# Revit family: 3034751 Lighting Fixture_Sylvania_Giotto 235 LED_Recessed Mounted
name_source: partatom
category: Lighting Fixtures
revit_build: Autodesk Revit 2015 (Build: 20140606_1530(x64)
units: mm (PartAtom-declared; Revit-internal decimal feet)

## types (1)
- Giotto235 rec ww EB
    Apparent Load = 12 VA
    Assembly Code = D5020200
    Body Material = Polycarbonate_Sylvania_Giotto_White
    Catalog Number = 3034751
    Color Filter = 16777215
    Cutout Diameter = 235 mm
    Default Elevation = 0 mm  [stored 0 ft]
    Description = Surface or recessed mount versions available Ideal for general lighting in public areas Microwave presence detection versions 3 hour emergency light versions with integrated gear Up to 1200lm neutral white
    Diffuser Material = Polycarbonate_Sylvania_Giotto_Opal
    Dimming Lamp Color Temperature Shift = <None>
    Drive Current = 700 mA
    Electrical Protection = CLASS I
    Emit Shape Visible in Rendering = No
    Emit from Circle Diameter = 219 mm
    Energy Class = A++A+A
    Glow Wire Test = 850 °C
    Height = 92 mm  [stored 0.301837 ft]
    IK Rating = IK10
    IP Rating = IP44
    Lamp = 12 W
    Lamp Comments = Integrated LED
    Life = 50 000 h
    Manufacturer = Feilo Sylvania
    Model = Giotto235 rec ww EB
    Photometric Web File = 3034751.ies
    Product Family = GIOTTO LED 235 - RECESSED
    Product Page URL = http://www.feilosylvania.com
    Tilt Angle = -90°
    URL = http://www.feilosylvania.com
    Voltage = 230 V
    Voltage Comments = UNV (Universal Voltage; 220-240 Volt)
    Weight = 1 kg
    Width = 265 mm  [stored 0.869423 ft]

note: [stored X ft] marks values corroborated as IEEE doubles in the binary element streams (Revit-internal decimal feet)

## geometry (parser evidence)
native form markers: Sweep x3
no freeform markers — native parametric forms only
